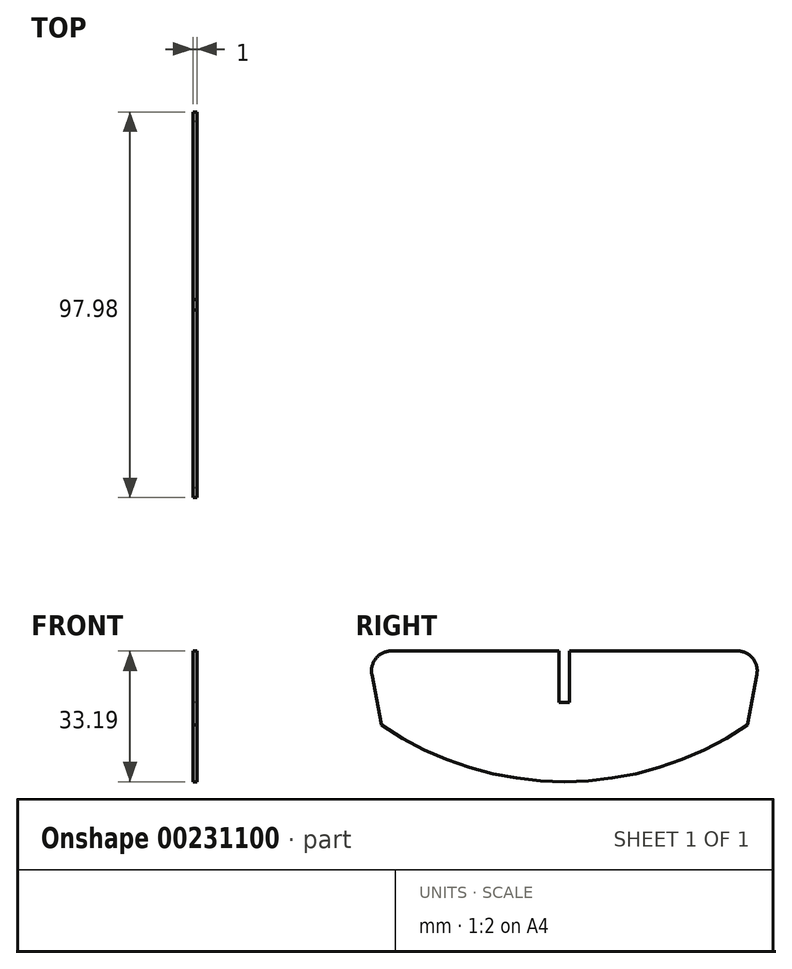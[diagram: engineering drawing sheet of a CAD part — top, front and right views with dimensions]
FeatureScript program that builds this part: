
annotation { "Feature Type Name" : "Feature", "Feature Type Description" : "" }
export const myFeature = defineFeature(function(context is Context, id is Id, definition is map)
    precondition{}
    {
        {
            var Q0;
            Q0=qCreatedBy(makeId("Right.planeOp"),FACE);
            var sketch = newSketch(context, id + "F0", { "sketchPlane" : qUnion([Q0])});
            skLineSegment(sketch, "E0", {"start": v(94.51, 56.36) * mm, "end": v(137.16, 56.36) * mm});
            skLineSegment(sketch, "E1", {"start": v(89.6, 50.45) * mm, "end": v(91.98, 37.54) * mm});
            skLineSegment(sketch, "E2", {"start": v(187.4, 50.45) * mm, "end": v(185.01, 37.54) * mm});
            skLineSegment(sketch, "E3", {"start": v(137.16, 43.36) * mm, "end": v(139.84, 43.36) * mm});
            skLineSegment(sketch, "E4", {"start": v(139.84, 56.36) * mm, "end": v(139.84, 43.36) * mm});
            skLineSegment(sketch, "E5", {"start": v(137.16, 56.36) * mm, "end": v(137.16, 43.36) * mm});
            skLineSegment(sketch, "E6", {"start": v(139.84, 56.36) * mm, "end": v(182.49, 56.36) * mm});
            skArc(sketch, "E7", {"start": v(94.51, 56.36) * mm, "mid": v(90.67, 54.56) * mm, "end": v(89.6, 50.45) * mm});
            skArc(sketch, "E8", {"start": v(187.4, 50.45) * mm, "mid": v(186.33, 54.56) * mm, "end": v(182.49, 56.36) * mm});
            skArc(sketch, "E9", {"start": v(91.98, 37.54) * mm, "mid": v(138.5, 23.17) * mm, "end": v(185.01, 37.54) * mm});
            skSolve(sketch);
        }
        {
            var Q0;
            Q0=makeQuery(id+"F0.imprint","IMPRINT",FACE,{"disambiguationData":[TD([[makeQuery(id+"F0.imprint","IMPRINT",EDGE,{"derivedFrom":sQuery(id+"F0.wireOp",EDGE,"E0")}),-1.0]])]});
            extrude(context, id + "F1", {"entities" : qUnion([Q0]), "depth" : 1 * mm});
        }
    });
